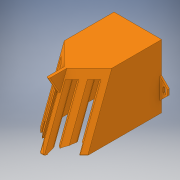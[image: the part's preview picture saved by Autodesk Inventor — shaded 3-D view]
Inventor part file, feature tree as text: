
AUTODESK INVENTOR PART (.ipt)
format: ipt  version: 2019 (Build 230136000, 136)  size: 399,360 bytes
history: native  units: in
note: dims shown in document units (in); Inventor stores cm internally (conversion verified against a paired STEP export)
features: extrude x18, sketch x15, plane x4, chamfer x3, other x2
ambient origin geometry x8: Origin, YZ Plane, XZ Plane, XY Plane, X Axis, Y Axis, Z Axis, Center Point
bodies: Solid1 (feature_tree)
feature tree (42):
  sketch  "Sketch1"  dims[d0=4.253in d1=90.0deg]
  other  "Work Axis1"
  plane  "Work Plane1"
  plane  "Work Plane2"
  extrude  "Extrusion1"  TaperAngle=90.0deg  [1 undecoded]
  extrude  "Extrusion2"  TaperAngle=180.0deg  [1 undecoded]
  sketch  "Sketch4"  dims[d6=45.0deg d7=135.0deg]
  extrude  "Extrusion3"  Depth=2.0in
  extrude  "Extrusion4"  TaperAngle=135.0deg  [1 undecoded]
  plane  "Work Plane3"
  extrude  "Extrusion5"  Depth=5.0in
  plane  "Work Plane4"
  extrude  "Extrusion6"  Depth=0.1181in TaperAngle=0.0deg
  extrude  "Extrusion7"  Depth=5.0in
  sketch  "Sketch9"  dims[d16=0.1181in d17=0.0in d18=1.0in]
  extrude  "Extrusion8"  Depth=1.0in
  extrude  "Extrusion9"  Depth=0.0787in
  extrude  "Extrusion10"  Depth=1.0in
  extrude  "Extrusion11"  Depth=0.0787in
  extrude  "Extrusion12"  Depth=2.0in
  sketch  "Sketch12"  dims[d21=2.877in d22=1.0in]
  extrude  "Extrusion14"  Depth=0.1181in TaperAngle=0.0deg
  chamfer  "Chamfer1"  Distance=8.0in
  extrude  "Extrusion15"  Depth=7.0in TaperAngle=0.0deg
  extrude  "Extrusion16"  Depth=0.125in TaperAngle=0.0deg
  extrude  "Extrusion17"  Depth=0.125in
  extrude  "Extrusion18"  TaperAngle=90.0deg  [1 undecoded]
  chamfer  "Chamfer3"  Distance=1.2992in
  extrude  "Extrusion19"  TaperAngle=45.0deg  [1 undecoded]
  chamfer  "Chamfer4"  Distance=1.7323in
  other  "Work Axis2"
  sketch  "Sketch2"  dims[d2=1.0in d3=180.0deg]
  sketch  "Sketch3"  dims[d4=2.0in d5=4.253in]
  sketch  "Sketch6"  dims[d8=75.0deg d9=105.0deg d10=5.0in]
  sketch  "Sketch7"  dims[d11=5.0in d12=0.1181in d13=0.0in]
  sketch  "Sketch8"  dims[d14=5.0in d15=5.0in]
  sketch  "Sketch11"  dims[d19=180.0deg d20=0.0787in]
  sketch  "Sketch13"  dims[d23=0.0in d24=0.0787in]
  sketch  "Sketch14"  dims[d25=2.877in d26=2.0in]
  sketch  "Sketch15"  dims[d27=0.0787in d28=0.1181in d29=0.0in d30=8.0in d31=0.0in]
  sketch  "Sketch16"  dims[d32=90.0deg d33=7.0in d34=0.0in]
  sketch  "Sketch17"  dims[d35=90.0deg d36=7.0in d37=0.0in d38=4.253in d39=90.0deg d40=1.2992in d41=45.0deg d42=1.7323in d43=0.0in d44=7.0in d45=0.0in d46=7.0in d47=0.0in d48=7.0in d49=0.0in d50=7.0in d51=0.0in d52=7.0in d53=0.0in d62=1.0in d63=90.0deg d64=1.0787in d65=90.0deg d66=0.3in d67=90.0deg d68=0.2in d69=0.0in d70=0.35in d71=0.6in d72=0.1in d73=90.0deg d74=0.1181in d75=0.0787in d76=0.0in d77=0.175in d78=0.125in d79=45.0deg d83=0.75in d84=90.0deg d85=150.0deg d86=0.1181in d87=0.0in d88=0.1181in d89=0.0in d90=0.1181in d91=0.0in d92=0.1181in d93=0.0in d94=0.0394in d95=0.125in d96=45.0deg d97=0.25in d98=0.0in d99=0.5in d100=180.0deg d101=0.25in d102=180.0deg d103=0.5in d104=180.0deg d105=0.0625in d106=0.0in d107=0.125in d108=2.5in d109=1.5748in d111=0.5in d112=0.3937in d114=1.0in d116=1.0in d117=0.0in d118=0.125in d119=0.125in d120=45.0deg]
note: 5 required parameter values undecoded (feature->parameter linkage not recoverable at this tier; creation-order binding heuristic only, values carry confidence <= 0.55)
